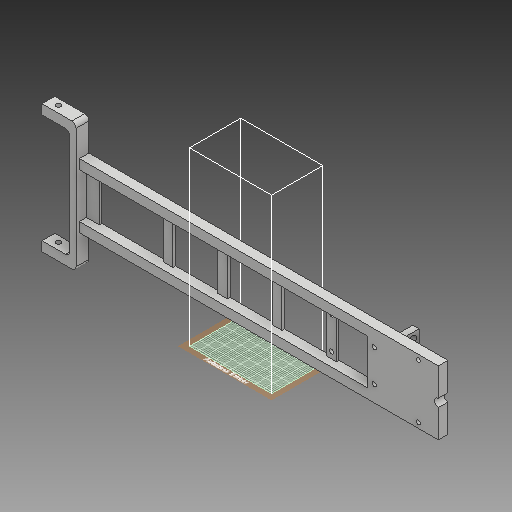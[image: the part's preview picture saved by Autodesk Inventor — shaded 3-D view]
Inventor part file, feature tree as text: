
AUTODESK INVENTOR PART (.ipt)
format: ipt  version: 2018 (Build 220112000, 112)  size: 874,496 bytes
history: native  units: mm
features: sketch x56, extrude x43, fillet x13, hole x6, plane x1
ambient origin geometry x8: Origin, YZ Plane, XZ Plane, XY Plane, X Axis, Y Axis, Z Axis, Center Point
bodies: Solid1 (feature_tree)
feature tree (119):
  extrude  "Extrusion1"  Depth=50.0mm
  hole  "Hole1"  [1 undecoded]
  hole  "Hole2"  [1 undecoded]
  extrude  "Extrusion2"  Depth=25.0mm
  extrude  "Extrusion3"  Depth=25.0mm
  extrude  "Extrusion4"  Depth=5.0mm
  sketch  "Sketch7"  dims[d25=10.0mm d26=5.0mm]
  extrude  "Extrusion5"  Depth=5.0mm
  extrude  "Extrusion6"  Depth=35.0mm
  extrude  "Extrusion7"  Depth=35.0mm
  extrude  "Extrusion8"  Depth=35.0mm
  extrude  "Extrusion9"  Depth=2.0mm TaperAngle=0.0deg
  extrude  "Extrusion10"  Depth=7.5mm TaperAngle=0.0deg
  extrude  "Extrusion11"  Depth=10.0mm
  extrude  "Extrusion12"  Depth=7.5mm
  fillet  "Fillet1"  Radius=7.5mm
  fillet  "Fillet2"  Radius=25.0mm
  fillet  "Fillet3"  Radius=3.0mm
  fillet  "Fillet4"  Radius=3.2mm
  fillet  "Fillet5"  Radius=2.1mm
  fillet  "Fillet6"  Radius=5.5mm
  extrude  "Extrusion13"  Depth=92.5mm TaperAngle=0.0deg
  sketch  "Sketch17"  dims[d58=4.25mm d59=241.0mm d60=0.0mm]
  hole  "Hole3"  [1 undecoded]
  hole  "Hole4"  [1 undecoded]
  extrude  "Extrusion14"  Depth=5.0mm
  extrude  "Extrusion15"  Depth=2.5mm TaperAngle=0.0deg
  extrude  "Extrusion16"  Depth=6.35mm
  extrude  "Extrusion17"  Depth=2.5mm
  extrude  "Extrusion18"  Depth=14.55mm TaperAngle=0.0deg
  extrude  "Extrusion19"  Depth=0.1mm
  extrude  "Extrusion20"  Depth=3.25mm
  extrude  "Extrusion21"  Depth=3.25mm
  hole  "Hole5"  [1 undecoded]
  extrude  "Extrusion22"  Depth=2.0mm
  extrude  "Extrusion23"  Depth=15.0mm
  extrude  "Extrusion24"  Depth=10.0mm TaperAngle=0.0deg
  hole  "Hole6"  [1 undecoded]
  extrude  "Extrusion25"  Depth=100.0mm TaperAngle=0.0deg
  extrude  "Extrusion26"  Depth=2.0mm TaperAngle=0.0deg
  sketch  "Sketch35"  dims[d116=3.3mm d117=3.3mm]
  plane  "Work Plane1"
  sketch  "Sketch36"  dims[d118=3.3mm d119=3.3mm d120=2.0mm d121=0.0mm]
  extrude  "Extrusion27"  Depth=3.3mm
  extrude  "Extrusion28"  Depth=2.0mm
  fillet  "Fillet7"  Radius=2.0mm
  extrude  "Extrusion29"  Depth=8.0mm
  extrude  "Extrusion30"  Depth=21.0mm
  extrude  "Extrusion31"  Depth=8.5mm
  extrude  "Extrusion32"  Depth=3.5mm
  sketch  "Sketch43"  dims[d142=10.0mm d143=0.0mm d144=7.5mm d145=0.0mm]
  fillet  "Fillet8"  Radius=3.3mm
  extrude  "Extrusion33"  Depth=3.3mm
  extrude  "Extrusion34"  Depth=7.5mm TaperAngle=0.0deg
  extrude  "Extrusion35"  Depth=15.0mm
  extrude  "Extrusion36"  Depth=100.0mm TaperAngle=0.0deg
  extrude  "Extrusion37"  Depth=5.0mm
  fillet  "Fillet9"  Radius=5.0mm
  fillet  "Fillet10"  Radius=37.5mm
  fillet  "Fillet11"  Radius=1.1mm
  fillet  "Fillet12"  Radius=37.5mm
  sketch  "Sketch49"  dims[d170=5.5mm d171=0.0mm d172=10.0mm d173=0.0mm]
  extrude  "Extrusion38"  Depth=0.2mm
  extrude  "Extrusion39"  Depth=10.0mm TaperAngle=0.0deg
  extrude  "Extrusion40"  Depth=74.724mm
  fillet  "Fillet13"  Radius=85.515mm
  extrude  "Extrusion41"  Depth=5.0mm
  extrude  "Extrusion42"  Depth=5.0mm
  sketch  "Sketch55"  dims[d184=2.0mm d185=0.0mm]
  extrude  "Extrusion43"  Depth=5.0mm
  sketch  "Sketch1"  dims[d0=50.0mm d1=50.0mm]
  sketch  "Sketch2"  dims[d2=240.0mm d3=7.5mm]
  sketch  "Sketch3"  dims[d4=7.5mm d5=7.5mm d6=0.0mm]
  sketch  "Sketch4"  dims[d7=6.35mm d8=6.0mm d9=4.0mm d10=2.0mm d11=90.0deg d12=8.0mm d13=20.594885mm d14=25.0mm]
  sketch  "Sketch5"  dims[d15=3.3mm d16=6.0mm d17=4.0mm d18=2.0mm d19=90.0deg d20=8.0mm d21=20.594885mm d22=25.0mm]
  sketch  "Sketch6"  dims[d23=180.0deg d24=5.0mm]
  sketch  "Sketch8"  dims[d27=17.5mm d28=0.0mm d30=35.0mm]
  sketch  "Sketch9"  dims[d31=35.0mm d32=35.0mm]
  sketch  "Sketch10"  dims[d33=35.0mm d34=35.0mm]
  sketch  "Sketch11"  dims[d35=35.0mm d36=2.0mm d37=0.0mm]
  sketch  "Sketch12"  dims[d38=10.0mm d39=7.5mm d40=0.0mm]
  sketch  "Sketch13"  dims[d41=100.0mm d42=10.0mm]
  sketch  "Sketch14"  dims[d43=7.5mm d44=0.0mm d45=7.5mm d46=7.5mm d47=25.0mm d48=0.0mm d49=3.0mm d50=3.2mm d51=2.1mm d52=5.5mm]
  sketch  "Sketch15"  dims[d53=3.3mm d54=92.5mm d55=0.0mm]
  sketch  "Sketch16"  dims[d56=5.5mm d57=3.3mm]
  sketch  "Sketch18"  dims[d61=4.44mm d62=5.0mm]
  sketch  "Sketch19"  dims[d63=2.5mm d64=91.25mm d65=0.0mm]
  sketch  "Sketch20"  dims[d66=30.0mm d67=6.35mm]
  sketch  "Sketch21"  dims[d68=3.8mm d69=0.0mm d70=2.5mm]
  sketch  "Sketch22"  dims[d71=14.55mm d72=0.0mm d73=14.55mm d74=0.0mm]
  sketch  "Sketch23"  dims[d75=0.1mm d76=0.1mm]
  sketch  "Sketch24"  dims[d77=3.25mm d78=3.25mm]
  sketch  "Sketch25"  dims[d79=3.25mm d80=3.25mm]
  sketch  "Sketch26"  dims[d81=35.0mm d82=10.0mm]
  sketch  "Sketch27"  dims[d83=2.0mm d84=0.0mm d85=3.6mm]
  sketch  "Sketch28"  dims[d86=3.6mm]
  sketch  "Sketch29"  dims[d87=3.3mm d88=6.0mm d89=4.0mm d90=2.0mm d91=90.0deg d92=15.0mm d93=20.594885mm]
  sketch  "Sketch30"  dims[d94=3.3mm d95=6.0mm d96=4.0mm d97=2.0mm d98=90.0deg d99=15.0mm d100=20.594885mm d101=6.0mm]
  sketch  "Sketch31"  dims[d102=20.0mm d103=0.0mm d104=10.0mm d105=0.0mm]
  sketch  "Sketch32"  dims[d106=2.0mm d107=0.0mm d108=4.0mm]
  sketch  "Sketch33"  dims[d109=100.0mm d110=0.0mm d111=100.0mm d112=0.0mm]
  sketch  "Sketch34"  dims[d113=5.0mm d114=2.0mm d115=0.0mm]
  sketch  "Sketch37"  dims[d122=5.5mm d123=0.0mm]
  sketch  "Sketch38"  dims[d124=3.3mm d125=6.0mm d126=4.0mm d127=2.0mm d128=90.0deg d129=8.0mm d130=20.594885mm d131=42.0mm]
  sketch  "Sketch39"  dims[d132=17.0mm d133=21.0mm]
  sketch  "Sketch40"  dims[d135=8.5mm d136=15.825mm]
  sketch  "Sketch41"  dims[d137=3.5mm d138=21.0mm d139=3.3mm]
  sketch  "Sketch42"  dims[d140=3.3mm d141=3.3mm]
  sketch  "Sketch44"  dims[d146=100.0mm d147=0.0mm]
  sketch  "Sketch45"  dims[d148=5.0mm d149=6.0mm d150=4.0mm d151=2.0mm d152=90.0deg d153=15.0mm d154=0.0mm d155=3.75mm]
  sketch  "Sketch46"  dims[d156=100.0mm d157=0.0mm d158=100.0mm d159=0.0mm]
  sketch  "Sketch47"  dims[d160=-0.698132mm d161=5.0mm d162=5.0mm d163=37.5mm d164=0.0mm d165=1.1mm d166=37.5mm d167=0.0mm]
  sketch  "Sketch48"  dims[d168=0.2mm d169=3.0mm]
  sketch  "Sketch50"  dims[d174=74.724mm d175=74.724mm d176=85.515mm]
  sketch  "Sketch51"  dims[d177=5.0mm d178=85.515mm]
  sketch  "Sketch52"  dims[d179=5.0mm d180=85.515mm]
  sketch  "Sketch53"  dims[d181=5.0mm d182=85.515mm]
  sketch  "Sketch54"  dims[d183=5.0mm]
  sketch  "Sketch56"  dims[d186=10.0mm d187=2.0mm d188=0.0mm d189=2.0mm d190=1.0mm d191=0.0mm d192=2.0mm d193=0.0mm d194=10.0mm d195=1.0mm d196=0.0mm d197=20.0mm d198=1.0mm d199=0.0mm d200=7.5mm d201=5.0mm d202=2.5mm d203=0.0mm d204=3.25mm d205=3.25mm d206=3.25mm d207=3.25mm d208=6.25mm d209=9.58mm d210=250.0mm d211=0.0mm d212=5.25mm d213=4.3mm d214=0.0mm d215=4.3mm d216=0.0mm d217=3.25mm d218=9.7mm d219=100.0mm d220=0.0mm d221=9.8mm d222=4.5mm d223=4.3mm d224=0.0mm d225=9.8mm d226=4.3mm d227=0.0mm]
note: 6 required parameter values undecoded (feature->parameter linkage not recoverable at this tier; creation-order binding heuristic only, values carry confidence <= 0.55)
